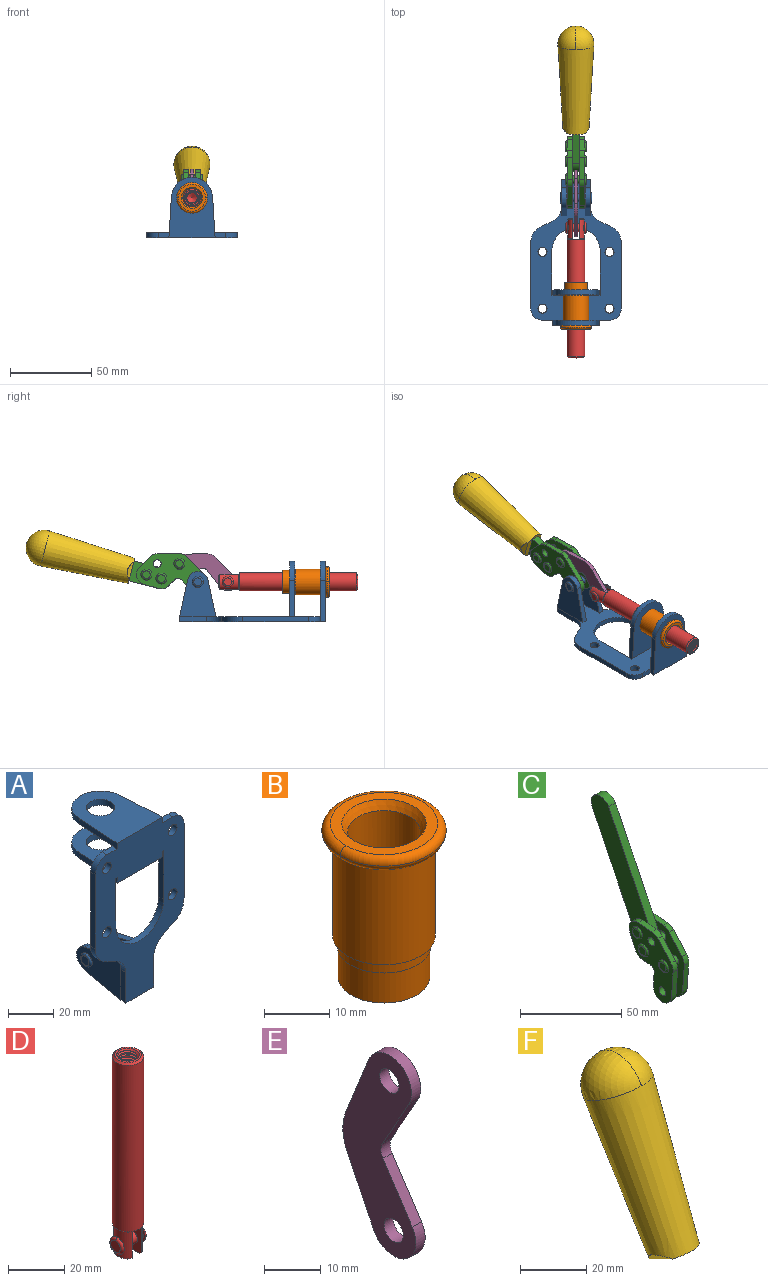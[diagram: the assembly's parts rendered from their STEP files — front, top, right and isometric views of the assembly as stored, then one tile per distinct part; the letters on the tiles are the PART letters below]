
ASSEMBLY  parts=6 mates=6
PART A: 55 faces, bbox 55.7x37.4x89.8 mm
  f0: torus R=2.41mm, axis (-1,0,0), area 15mm2, adj f11,f15,f25
  f1: torus R=2.41mm, axis (-1,0,0), area 15mm2, adj f10,f12,f22
  f2: cylinder r=2.78mm len=5.56mm, axis (0,-1,0), area 54.2mm2, adj f30,f54
  f3: cylinder r=14.99mm len=29.97mm, axis (0,-1,0), area 145.9mm2, adj f30,f49,f53,f54
  f4: cylinder r=2.78mm len=5.56mm, axis (0,-1,0), area 54.2mm2, adj f30,f54
  f5: cylinder r=2.78mm len=5.56mm, axis (0,-1,0), area 54.2mm2, adj f30,f54
  f6: cylinder r=2.78mm len=5.56mm, axis (0,-1,0), area 54.2mm2, adj f30,f54
  f7: cylinder r=6.35mm len=12.7mm, axis (0,0,1), area 123.6mm2, adj f27,f51
  f8: cylinder r=6.35mm len=12.7mm, axis (0,0,-1), area 124.7mm2, adj f21,f35
  f9: cylinder r=2.41mm len=11.18mm, axis (-1,0,0), area 169.4mm2, adj f16,f19
  f10: plane 4.83x4.83mm, normal (1,0,0), area 18.3mm2, adj f1,f12
  f11: plane 4.83x4.83mm, normal (-1,0,0), area 18.3mm2, adj f0,f15
  f12: torus R=2.41mm, axis (-1,0,0), area 15mm2, adj f1,f10,f22
  f13: cylinder r=6.35mm len=12.41mm, axis (1,0,0), area 53.4mm2, adj f18,f19,f22,f23
  f14: cylinder r=6.35mm len=12.41mm, axis (-1,0,0), area 53.4mm2, adj f16,f17,f24,f25
  f15: torus R=2.41mm, axis (-1,0,0), area 15mm2, adj f0,f11,f25
  f16: plane 27.86x22.35mm, normal (1,0,0), area 425.4mm2, adj f9,f14,f17,f24,f30
  f17: plane 22.86x4.97mm, normal (0,0.21,0.98), area 72.5mm2, adj f14,f16,f25,f30
  f18: plane 22.86x4.97mm, normal (0,0.21,0.98), area 72.5mm2, adj f13,f19,f22,f30
  f19: plane 27.86x22.35mm, normal (-1,0,0), area 425.4mm2, adj f9,f13,f18,f23,f30
  f20: cylinder r=12.7mm len=25.35mm, axis (0,0,-1), area 119.8mm2, adj f21,f34,f35,f36
  f21: plane 34.21x28.07mm, normal (0,0,-1), area 702.4mm2, adj f8,f20,f30,f34,f36
  f22: plane 27.96x22.45mm, normal (1,0,0), area 407.2mm2, adj f1,f12,f13,f18,f23,f30,f42,f43
  f23: plane 22.86x4.97mm, normal (0,0.21,-0.98), area 72.5mm2, adj f13,f19,f22,f44
  f24: plane 22.86x4.97mm, normal (0,0.21,-0.98), area 72.5mm2, adj f14,f16,f25,f44
  f25: plane 27.86x22.35mm, normal (-1,0,0), area 407.1mm2, adj f0,f14,f15,f17,f24,f30,f45,f46
  f26: plane 3.1x0.95mm, normal (0,0,-1), area 2.7mm2, adj f30,f49,f50,f54
  f27: plane 34.21x28.07mm, normal (0,0,1), area 702.4mm2, adj f7,f28,f30,f50,f52
  f28: cylinder r=12.7mm len=25.35mm, axis (0,0,1), area 118.8mm2, adj f27,f50,f51,f52
  f29: plane 3.1x0.95mm, normal (0,0,-1), area 2.7mm2, adj f30,f52,f53,f54
  f30: plane 86.54x55.63mm, normal (0,1,0), area 2362.9mm2, adj f2,f3,f4,f5,f6,f16,f17,f18
  f31: plane 40.56x3.1mm, normal (-1,0,0), area 125.7mm2, adj f30,f32,f48,f54
  f32: cylinder r=7.11mm len=7.11mm, axis (0,-1,0), area 34.6mm2, adj f30,f31,f33,f54
  f33: plane 6.67x3.1mm, normal (0,0,1), area 20.4mm2, adj f30,f32,f34,f54
  f34: plane 25.39x3.13mm, normal (-1,0.06,0), area 79.5mm2, adj f20,f21,f33,f35,f54
  f35: plane 37.31x28.45mm, normal (0,0,1), area 789.9mm2, adj f8,f20,f34,f36,f54
  f36: plane 25.39x3.13mm, normal (1,0.06,0), area 79.5mm2, adj f20,f21,f35,f37,f54
  f37: plane 6.67x3.1mm, normal (0,0,1), area 20.4mm2, adj f30,f36,f38,f54
  f38: cylinder r=7.11mm len=7.11mm, axis (0,-1,0), area 34.6mm2, adj f30,f37,f39,f54
  f39: plane 40.56x3.1mm, normal (1,0,0), area 125.7mm2, adj f30,f38,f40,f54
  f40: cylinder r=11.18mm len=10.16mm, axis (0,-1,0), area 39.5mm2, adj f30,f39,f41,f54
  f41: plane 6.09x3.1mm, normal (0.42,0,-0.91), area 20.8mm2, adj f30,f40,f42,f54
  f42: cylinder r=11.18mm len=9.41mm, axis (0,-1,0), area 37.2mm2, adj f22,f30,f41,f43,f54
  f43: plane 16.5x3.1mm, normal (1,0,0), area 51.1mm2, adj f22,f42,f44,f54
  f44: plane 17.37x3.1mm, normal (0,0,-1), area 53.8mm2, adj f23,f24,f30,f43,f45,f54
  f45: plane 16.5x3.1mm, normal (-1,0,0), area 51.1mm2, adj f25,f44,f46,f54
  f46: cylinder r=11.18mm len=9.41mm, axis (0,-1,0), area 37.2mm2, adj f25,f30,f45,f47,f54
  f47: plane 6.09x3.1mm, normal (-0.42,0,-0.91), area 20.8mm2, adj f30,f46,f48,f54
  f48: cylinder r=11.18mm len=10.16mm, axis (0,-1,0), area 39.5mm2, adj f30,f31,f47,f54
  f49: plane 26.54x3.1mm, normal (-1,0,0), area 82.3mm2, adj f3,f26,f30,f54
  f50: plane 25.39x3.1mm, normal (1,0.06,0), area 78.8mm2, adj f26,f27,f28,f51,f54
  f51: plane 37.31x28.45mm, normal (0,0,-1), area 789.9mm2, adj f7,f28,f50,f52,f54
  f52: plane 25.39x3.1mm, normal (-1,0.06,0), area 78.8mm2, adj f27,f28,f29,f51,f54
  f53: plane 26.54x3.1mm, normal (1,0,0), area 82.3mm2, adj f3,f29,f30,f54
  f54: plane 89.66x55.63mm, normal (0,-1,0), area 2678.5mm2, adj f2,f3,f4,f5,f6,f26,f29,f31
PART B: 15 faces, bbox 20.6x20.6x28.7 mm
  f0: torus R=8.26mm, axis (0,0,1), area 56.8mm2, adj f1,f10,f12
  f1: torus R=8.26mm, axis (0,0,1), area 56.8mm2, adj f0,f6,f13
  f2: cylinder r=5.59mm len=25.91mm, axis (0,0,1), area 909.6mm2, adj f3,f4
  f3: cone r=6.86mm half-angle=45deg, axis (0,0,-1), area 70.2mm2, adj f2,f14
  f4: cone r=6.47mm half-angle=30deg, axis (0,0,1), area 66.7mm2, adj f2,f13
  f5: cylinder r=7.04mm len=14.07mm, axis (0,0,1), area 252.6mm2, adj f11,f14
  f6: torus R=8.26mm, axis (0,0,1), area 56.8mm2, adj f1,f12,f13
  f7: cylinder r=7.16mm len=14.33mm, axis (0,0,1), area 91.5mm2, adj f9,f11
  f8: cylinder r=7.86mm len=18.42mm, axis (0,0,1), area 909.6mm2, adj f9,f10
  f9: plane 15.72x15.72mm, normal (0,0,-1), area 33mm2, adj f7,f8
  f10: plane 16.51x16.51mm, normal (0,0,-1), area 19.9mm2, adj f0,f8,f12
  f11: plane 14.33x14.33mm, normal (0,0,-1), area 5.7mm2, adj f5,f7
  f12: torus R=8.26mm, axis (0,0,1), area 56.8mm2, adj f0,f6,f10
  f13: plane 16.51x16.51mm, normal (0,0,1), area 82.7mm2, adj f1,f4,f6
  f14: plane 14.07x14.07mm, normal (0,0,-1), area 7.8mm2, adj f3,f5
PART C: 59 faces, bbox 12.9x60.2x99.6 mm
  f0: torus R=2.39mm, axis (-1,0,0), area 14.9mm2, adj f20,f43,f51
  f1: torus R=2.39mm, axis (-1,0,0), area 14.9mm2, adj f19,f42,f51
  f2: torus R=2.39mm, axis (-1,0,0), area 14.9mm2, adj f18,f35,f51
  f3: torus R=2.39mm, axis (-1,0,0), area 14.9mm2, adj f14,f17,f23
  f4: torus R=2.39mm, axis (-1,0,0), area 14.9mm2, adj f13,f16,f23
  f5: torus R=2.39mm, axis (-1,0,0), area 14.9mm2, adj f12,f15,f23
  f6: cylinder r=2.39mm len=4.78mm, axis (1,0,0), area 46.5mm2, adj f48,f50,f51
  f7: cylinder r=2.39mm len=4.78mm, axis (1,0,0), area 46.5mm2, adj f50,f51
  f8: cylinder r=6.35mm len=12.68mm, axis (1,0,0), area 61.8mm2, adj f38,f39,f50,f51
  f9: cylinder r=2.39mm len=4.78mm, axis (-1,0,0), area 70.5mm2, adj f46,f50
  f10: cylinder r=2.39mm len=4.78mm, axis (-1,0,0), area 46.5mm2, adj f23,f45,f46
  f11: cylinder r=2.39mm len=4.78mm, axis (-1,0,0), area 46.5mm2, adj f23,f46
  f12: plane 4.78x4.78mm, normal (1,0,0), area 17.9mm2, adj f5,f15
  f13: plane 4.78x4.78mm, normal (1,0,0), area 17.9mm2, adj f4,f16
  f14: plane 4.78x4.78mm, normal (1,0,0), area 17.9mm2, adj f3,f17
  f15: torus R=2.39mm, axis (-1,0,0), area 14.9mm2, adj f5,f12,f23
  f16: torus R=2.39mm, axis (-1,0,0), area 14.9mm2, adj f4,f13,f23
  f17: torus R=2.39mm, axis (-1,0,0), area 14.9mm2, adj f3,f14,f23
  f18: plane 4.78x4.78mm, normal (-1,0,0), area 17.9mm2, adj f2,f35
  f19: plane 4.78x4.78mm, normal (-1,0,0), area 17.9mm2, adj f1,f42
  f20: plane 4.78x4.78mm, normal (-1,0,0), area 17.9mm2, adj f0,f43
  f21: plane 2.26x0.2mm, normal (1,0,0), area 0.2mm2, adj f31,f44
  f22: plane 2.26x0.2mm, normal (-1,0,0), area 0.2mm2, adj f41,f44
  f23: plane 39.37x30.77mm, normal (1,0,0), area 565.5mm2, adj f3,f4,f5,f10,f11,f15,f16,f17
  f24: cylinder r=6.1mm len=4.15mm, axis (-1,0,0), area 14.7mm2, adj f23,f25,f32,f46
  f25: plane 10.25x9.01mm, normal (0,-0.75,0.66), area 42.3mm2, adj f23,f24,f26,f46
  f26: cylinder r=6.35mm len=4.64mm, axis (-1,0,0), area 15.6mm2, adj f23,f25,f27,f46
  f27: plane 15.84x3.1mm, normal (0,-1,-0.07), area 49.2mm2, adj f23,f26,f28,f46
  f28: cylinder r=6.35mm len=12.68mm, axis (-1,0,0), area 61.8mm2, adj f23,f27,f29,f46
  f29: plane 8.11x3.1mm, normal (0,1,0.07), area 25.2mm2, adj f23,f28,f30,f46
  f30: cylinder r=3.05mm len=3.25mm, axis (-1,0,0), area 14.8mm2, adj f23,f29,f31,f46
  f31: plane 5.99x3.1mm, normal (0,0.07,-1), area 18.6mm2, adj f21,f23,f30,f44,f46
  f32: plane 9.5x3.1mm, normal (0,-0.07,1), area 29.5mm2, adj f23,f24,f33,f46,f47
  f33: cylinder r=6.1mm len=8.63mm, axis (-1,0,0), area 39.1mm2, adj f23,f32,f34,f47
  f34: plane 8.65x3.96mm, normal (0,0.91,-0.42), area 29.5mm2, adj f23,f33,f44,f47
  f35: torus R=2.39mm, axis (-1,0,0), area 14.9mm2, adj f2,f18,f51
  f36: plane 10.25x9.01mm, normal (0,-0.75,0.66), area 42.3mm2, adj f37,f49,f50,f51
  f37: cylinder r=6.35mm len=4.64mm, axis (1,0,0), area 15.6mm2, adj f36,f38,f50,f51
  f38: plane 15.84x3.1mm, normal (0,-1,-0.07), area 49.2mm2, adj f8,f37,f50,f51
  f39: plane 8.11x3.1mm, normal (0,1,0.07), area 25.2mm2, adj f8,f40,f50,f51
  f40: cylinder r=3.05mm len=3.25mm, axis (1,0,0), area 14.8mm2, adj f39,f41,f50,f51
  f41: plane 5.99x3.1mm, normal (0,0.07,-1), area 18.6mm2, adj f22,f40,f44,f50,f51
  f42: torus R=2.39mm, axis (-1,0,0), area 14.9mm2, adj f1,f19,f51
  f43: torus R=2.39mm, axis (-1,0,0), area 14.9mm2, adj f0,f20,f51
  f44: cylinder r=6.35mm len=12.12mm, axis (-1,0,0), area 128.9mm2, adj f21,f22,f23,f31,f34,f41,f46,f47
  f45: plane 2.65x1.35mm, normal (1,0,0), area 1mm2, adj f10,f55
  f46: plane 39.08x20.42mm, normal (-1,0,0), area 412.5mm2, adj f9,f10,f11,f24,f25,f26,f27,f28
  f47: plane 77.62x39.82mm, normal (1,0,0), area 850mm2, adj f32,f33,f34,f44,f53,f54,f55
  f48: plane 2.65x1.35mm, normal (-1,0,0), area 1mm2, adj f6,f55
  f49: cylinder r=6.1mm len=4.15mm, axis (1,0,0), area 14.7mm2, adj f36,f50,f51,f56
  f50: plane 39.08x20.42mm, normal (1,0,0), area 412.5mm2, adj f6,f7,f8,f9,f36,f37,f38,f39
  f51: plane 39.37x30.77mm, normal (-1,0,0), area 565.5mm2, adj f0,f1,f2,f6,f7,f8,f35,f36
  f52: plane 8.65x3.96mm, normal (0,0.91,-0.42), area 29.5mm2, adj f44,f51,f57,f58
  f53: plane 68.49x33.4mm, normal (0,0.9,-0.44), area 358.1mm2, adj f44,f47,f54,f58
  f54: cylinder r=6.35mm len=12.06mm, axis (1,0,0), area 93.7mm2, adj f47,f53,f55,f58
  f55: plane 68.49x33.4mm, normal (0,-0.9,0.44), area 358.1mm2, adj f44,f45,f46,f47,f48,f50,f54,f58
  f56: plane 9.5x3.1mm, normal (0,-0.07,1), area 29.5mm2, adj f49,f50,f51,f57,f58
  f57: cylinder r=6.1mm len=8.63mm, axis (1,0,0), area 39.1mm2, adj f51,f52,f56,f58
  f58: plane 77.62x39.82mm, normal (-1,0,0), area 850mm2, adj f44,f52,f53,f54,f55,f56,f57
PART D: 48 faces, bbox 12.6x11.1x86.1 mm
  f0: torus R=2.41mm, axis (-1,0,0), area 15mm2, adj f30,f32,f34
  f1: torus R=2.41mm, axis (-1,0,0), area 15mm2, adj f29,f31,f33
  f2: cylinder r=5.54mm len=72.39mm, axis (0,0,1), area 2518.5mm2, adj f3,f4,f42,f43
  f3: cone r=5.54mm half-angle=45deg, axis (0,0,1), area 7.6mm2, adj f2,f5,f41
  f4: cone r=5.54mm half-angle=45deg, axis (0,0,-1), area 34.9mm2, adj f2,f39
  f5: cylinder r=5.08mm len=11.48mm, axis (0,0,1), area 108.3mm2, adj f3,f7,f8,f41
  f6: cylinder r=2.41mm len=4.83mm, axis (-1,0,0), area 71.2mm2, adj f40,f41
  f7: cylinder r=2.41mm len=4.83mm, axis (-1,0,0), area 7.6mm2, adj f5,f34
  f8: cone r=5.08mm half-angle=45deg, axis (0,0,1), area 10.6mm2, adj f5,f37,f41
  f9: cone r=3.98mm half-angle=45deg, axis (0,0,1), area 17.6mm2, adj f27,f39,f45,f46,f47
  f10: cylinder r=2.41mm len=4.83mm, axis (-1,0,0), area 7.6mm2, adj f33,f38
  f11: cylinder r=3.2mm len=6.4mm, axis (0,0,1), area 78.4mm2, adj f12,f28,f44,f45,f47
  f12: cylinder r=3.2mm len=6.4mm, axis (0,0,1), area 10.5mm2, adj f11,f13,f45,f47
  f13: cylinder r=3.2mm len=6.4mm, axis (0,0,1), area 10.5mm2, adj f12,f14,f45,f47
  f14: cylinder r=3.2mm len=6.4mm, axis (0,0,1), area 10.5mm2, adj f13,f15,f45,f47
  f15: cylinder r=3.2mm len=6.4mm, axis (0,0,1), area 10.5mm2, adj f14,f16,f45,f47
  f16: cylinder r=3.2mm len=6.4mm, axis (0,0,1), area 10.5mm2, adj f15,f17,f45,f47
  f17: cylinder r=3.2mm len=6.4mm, axis (0,0,1), area 10.5mm2, adj f16,f18,f45,f47
  f18: cylinder r=3.2mm len=6.4mm, axis (0,0,1), area 10.5mm2, adj f17,f19,f45,f47
  f19: cylinder r=3.2mm len=6.4mm, axis (0,0,1), area 10.5mm2, adj f18,f20,f45,f47
  f20: cylinder r=3.2mm len=6.4mm, axis (0,0,1), area 10.5mm2, adj f19,f21,f45,f47
  f21: cylinder r=3.2mm len=6.4mm, axis (0,0,1), area 10.5mm2, adj f20,f22,f45,f47
  f22: cylinder r=3.2mm len=6.4mm, axis (0,0,1), area 10.5mm2, adj f21,f23,f45,f47
  f23: cylinder r=3.2mm len=6.4mm, axis (0,0,1), area 10.5mm2, adj f22,f24,f45,f47
  f24: cylinder r=3.2mm len=6.4mm, axis (0,0,1), area 10.5mm2, adj f23,f25,f45,f47
  f25: cylinder r=3.2mm len=6.4mm, axis (0,0,1), area 10.5mm2, adj f24,f26,f45,f47
  f26: cylinder r=3.2mm len=6.4mm, axis (0,0,1), area 10.5mm2, adj f25,f27,f45,f47
  f27: cylinder r=3.2mm len=6.4mm, axis (0,0,1), area 7.4mm2, adj f9,f26,f45,f47
  f28: cone r=3.2mm half-angle=60deg, axis (0,0,1), area 37.2mm2, adj f11
  f29: plane 4.83x4.83mm, normal (-1,0,0), area 18.3mm2, adj f1,f31
  f30: plane 4.83x4.83mm, normal (1,0,0), area 18.3mm2, adj f0,f32
  f31: torus R=2.41mm, axis (-1,0,0), area 15mm2, adj f1,f29,f33
  f32: torus R=2.41mm, axis (-1,0,0), area 15mm2, adj f0,f30,f34
  f33: plane 6.83x6.83mm, normal (1,0,0), area 18.3mm2, adj f1,f10,f31
  f34: plane 6.83x6.83mm, normal (-1,0,0), area 18.3mm2, adj f0,f7,f32
  f35: cone r=5.08mm half-angle=45deg, axis (0,0,1), area 10.6mm2, adj f36,f38,f40
  f36: plane 7.25x1.97mm, normal (0,0,-1), area 10mm2, adj f35,f40
  f37: plane 7.25x1.97mm, normal (0,0,-1), area 10mm2, adj f8,f41
  f38: cylinder r=5.08mm len=11.48mm, axis (0,0,1), area 108.3mm2, adj f10,f35,f40,f42
  f39: plane 9.55x9.55mm, normal (0,0,1), area 22mm2, adj f4,f9
  f40: plane 12.76x10.09mm, normal (1,0,0), area 95.7mm2, adj f6,f35,f36,f38,f42,f43
  f41: plane 12.76x10.09mm, normal (-1,0,0), area 95.7mm2, adj f3,f5,f6,f8,f37,f43
  f42: cone r=5.54mm half-angle=45deg, axis (0,0,1), area 7.6mm2, adj f2,f38,f40
  f43: plane 11.07x4.7mm, normal (0,0,-1), area 50.4mm2, adj f2,f40,f41
  f44: plane 0.89x0.62mm, normal (-1,0,0), area 0.3mm2, adj f11,f45,f46,f47
  f45: bspline ~24.8x7.63mm, area 266.6mm2, adj f9,f11,f12,f13,f14,f15,f16,f17
  f46: bspline ~24.87x7.63mm, area 73.6mm2, adj f9,f44,f45,f47
  f47: bspline ~24.98x7.63mm, area 272.5mm2, adj f9,f11,f12,f13,f14,f15,f16,f17
PART E: 12 faces, bbox 2.3x18.2x42.8 mm
  f0: cylinder r=2.4mm len=4.8mm, axis (1,0,0), area 34.9mm2, adj f4,f11
  f1: cylinder r=10.41mm len=8.47mm, axis (1,0,0), area 20.2mm2, adj f4,f9,f10,f11
  f2: cylinder r=3.05mm len=3.16mm, axis (1,0,0), area 7.7mm2, adj f4,f6,f7,f11
  f3: cylinder r=2.4mm len=4.8mm, axis (1,0,0), area 34.9mm2, adj f4,f11
  f4: plane 42.81x18.23mm, normal (-1,0,0), area 414.1mm2, adj f0,f1,f2,f3,f5,f6,f7,f8
  f5: cylinder r=5.54mm len=10.67mm, axis (1,0,0), area 41.8mm2, adj f4,f6,f10,f11
  f6: plane 11.66x6.53mm, normal (0,-0.87,-0.49), area 30.9mm2, adj f2,f4,f5,f11
  f7: plane 11.17x7.33mm, normal (0,-0.84,0.55), area 30.9mm2, adj f2,f4,f8,f11
  f8: cylinder r=5.54mm len=10.51mm, axis (1,0,0), area 41.8mm2, adj f4,f7,f9,f11
  f9: plane 13.67x6.67mm, normal (0,0.9,-0.44), area 35.1mm2, adj f1,f4,f8,f11
  f10: plane 14.1x5.7mm, normal (0,0.93,0.37), area 35.1mm2, adj f1,f4,f5,f11
  f11: plane 42.81x18.23mm, normal (1,0,0), area 414.1mm2, adj f0,f1,f2,f3,f5,f6,f7,f8
PART F: 11 faces, bbox 22.3x42.6x64.5 mm
  f0: sphere r=11.13mm, area 411.4mm2, adj f1,f8
  f1: cone r=11.11mm half-angle=3.3deg, axis (0,0.44,0.9), area 3251.8mm2, adj f0,f7,f8,f9,f10
  f2: cylinder r=6.16mm len=11.7mm, axis (1,0,0), area 89.5mm2, adj f3,f4,f5,f6
  f3: plane 60.23x36.75mm, normal (-1,0,0), area 763.6mm2, adj f2,f4,f6,f10
  f4: plane 51.37x25.05mm, normal (0,0.9,-0.44), area 264.2mm2, adj f2,f3,f5,f10
  f5: plane 60.23x36.75mm, normal (1,0,0), area 763.6mm2, adj f2,f4,f6,f10
  f6: plane 51.37x25.05mm, normal (0,-0.9,0.44), area 264.2mm2, adj f2,f3,f5,f10
  f7: plane 9.95x5.95mm, normal (0.71,-0.31,-0.64), area 25.8mm2, adj f1,f10
  f8: sphere r=11.13mm, area 411.4mm2, adj f0,f1
  f9: plane 9.95x5.95mm, normal (-0.71,-0.31,-0.64), area 25.8mm2, adj f1,f10
  f10: plane 14.27x11.38mm, normal (0,-0.44,-0.9), area 106.7mm2, adj f1,f3,f4,f5,f6,f7,f9
PLACE A rot(axis=(1,0,0),90deg) t=(0,9.14,0)mm fixed
PLACE B rot(axis=(1,0,0),90deg) t=(0,9.14,0)mm
PLACE C rot(axis=(-1,0,0),49.5deg) t=(0,49.66,64.17)mm
PLACE D rot(axis=(1,0,0),90deg) t=(0,38.3,0)mm
PLACE E rot(axis=(1,0,0),112.5deg) t=(0,46.54,7.8)mm
PLACE F rot(axis=(-1,0,0),49.5deg) t=(-0.04,49.66,64.17)mm
MATE fastened F.f2 <-> C.f54  axis (1,0,0) through (-2.35,137.44,45.7)mm
MATE revolute D.f6 <-> E.f5  axis (-1,0,0) through (0,22.82,24.61)mm
MATE revolute C.f4 <-> E.f3  axis (-1,0,0) through (0,52.56,35.74)mm
MATE fastened B.f0 <-> A.f7  axis (0,1,0) through (0,-37.25,24.61)mm
MATE revolute A.f0 <-> C.f7  axis (-1,0,0) through (0,41.23,24.61)mm
MATE slider D.f2 <-> A.f7  axis (0,-1,0) through (0,-20.49,24.61)mm
